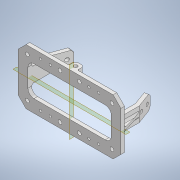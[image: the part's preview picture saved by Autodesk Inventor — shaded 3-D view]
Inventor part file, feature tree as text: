
AUTODESK INVENTOR PART (.ipt)
format: ipt  version: 2023 (Build 270158000, 158)  size: 560,640 bytes
history: native  units: mm
features: sketch x11, projected_geometry x11, other x11, extrude x9, thicken_offset x8, fillet x6, reference x6, mirror x5, chamfer x3, plane x2, hole x1
ambient origin geometry x8: Origin, YZ Plane, XZ Plane, XY Plane, X Axis, Y Axis, Z Axis, Center Point
bodies: Solid1 (feature_tree)
feature tree (73):
  extrude  "Extrusion1"  Depth=55.0mm
  extrude  "Extrusion2"  Depth=55.0mm
  thicken_offset  "Thicken1"
  thicken_offset  "Thicken2"
  thicken_offset  "Thicken3"
  thicken_offset  "Thicken4"
  plane  "Work Plane1"
  sketch  "Sketch3"  dims[d4=10.0mm d5=49.0mm]
  plane  "Work Plane2"
  extrude  "Extrusion3"  Depth=10.0mm
  extrude  "Extrusion4"  Depth=10.0mm
  mirror  "Mirror1"
  extrude  "Extrusion5"  Depth=3.0mm
  mirror  "Mirror2"
  extrude  "Extrusion6"  Depth=2.0mm
  mirror  "Mirror3"
  extrude  "Extrusion7"  Depth=2.0mm
  mirror  "Mirror4"
  extrude  "Extrusion8"  Depth=2.0mm
  mirror  "Mirror5"
  chamfer  "Chamfer2"  Distance=3.0mm
  fillet  "Fillet1"  Radius=5.0mm
  fillet  "Fillet2"  Radius=10.0mm
  chamfer  "Chamfer3"  Distance=5.0mm
  hole  "Hole1"  [1 undecoded]
  fillet  "Fillet3"  Radius=3.0mm
  fillet  "Fillet4"  Radius=3.0mm
  chamfer  "Chamfer4"  Distance=12.0mm
  thicken_offset  "Thicken5"
  thicken_offset  "Thicken6"
  thicken_offset  "Thicken7"
  thicken_offset  "Thicken8"
  fillet  "Fillet5"  Radius=2.0mm
  extrude  "Extrusion9"  Depth=3.0mm
  fillet  "Fillet6"  Radius=8.0mm
  sketch  "Sketch1"  dims[d0=12.0mm d1=55.0mm]
  reference  "Reference1"
  reference  "Reference2"
  reference  "Reference3"
  reference  "Reference4"
  sketch  "Sketch2"  dims[d2=12.0mm d3=55.0mm]
  projected_geometry  "Projected Loop1"
  sketch  "Sketch4"  dims[d6=10.0mm d7=49.0mm]
  reference  "Reference5"
  reference  "Reference6"
  projected_geometry  "Projected Loop2"
  sketch  "Sketch5"  dims[d8=3.0mm d9=0.0mm d10=2.0mm]
  projected_geometry  "Projected Loop3"
  projected_geometry  "Projected Loop4"
  sketch  "Sketch6"  dims[d11=2.0mm d12=2.0mm]
  projected_geometry  "Projected Loop5"
  projected_geometry  "Projected Loop6"
  sketch  "Sketch7"  dims[d13=2.0mm d14=2.0mm]
  projected_geometry  "Projected Loop7"
  sketch  "Sketch8"  dims[d15=2.0mm d16=2.0mm]
  projected_geometry  "Projected Loop8"
  sketch  "Sketch9"  dims[d17=2.0mm d18=3.0mm d19=0.0mm d20=5.0mm d21=10.0mm d22=7.0mm d23=10.0mm d24=5.0mm d25=7.0mm]
  projected_geometry  "Projected Loop9"
  sketch  "Sketch10"  dims[d26=7.0mm d27=7.0mm d28=3.0mm d29=3.0mm d30=12.0mm d31=0.0mm d32=2.0mm d33=0.0mm]
  projected_geometry  "Projected Loop10"
  sketch  "Sketch11"  dims[d34=2.0mm d35=0.0mm d36=4.0mm d37=8.0mm d38=3.1mm d39=3.1mm d40=2.0mm d41=0.0mm d45=8.0mm d46=8.0mm d47=3.1mm d48=3.1mm d49=10.0mm d50=0.0mm d51=2.0mm d52=7.0mm d53=7.0mm d54=3.1mm d55=5.0mm d56=0.0mm d57=1.5mm d58=2.0mm d59=45.0deg d60=2.0mm d61=5.0mm d62=8.0mm d63=2.0mm d64=45.0deg d65=33.0mm d66=70.0mm d67=3.1mm d68=6.0mm d69=4.0mm d70=2.0mm d71=90.0deg d72=20.0mm d73=0.0mm d74=2.0mm d75=1.5mm d76=2.0mm d77=2.0mm d78=45.0deg d79=1.5mm d80=1.5mm d81=1.5mm d82=1.5mm d83=1.5mm d84=1.5mm d85=1.5mm d86=1.5mm d87=1.0mm d88=6.0mm d89=25.0mm d90=10.0mm d91=0.0mm d92=3.0mm]
  projected_geometry  "Projected Loop11"
  parser-record x1  (decoder bookkeeping rows leaked as tree rows — omitted from the tree; the rows remain in map.json)
  other  "body_1.iam"
  other  "leg_1:1"
  other  "reducer_1:3"
  other  "mot_holder_1:1"
  other  "leg_1_MIR:1"
  other  "reducer_1_MIR:3"
  other  "mot_holder_1_MIR:1"
  other  "leg_1_MIR:2"
  other  "leg_1:2"
  other  "body_shell_2:1"
note: 1 required parameter value undecoded (feature->parameter linkage not recoverable at this tier; creation-order binding heuristic only, values carry confidence <= 0.55)
note: 1 file-system path scrubbed to <path> (originals preserved in map.json)
